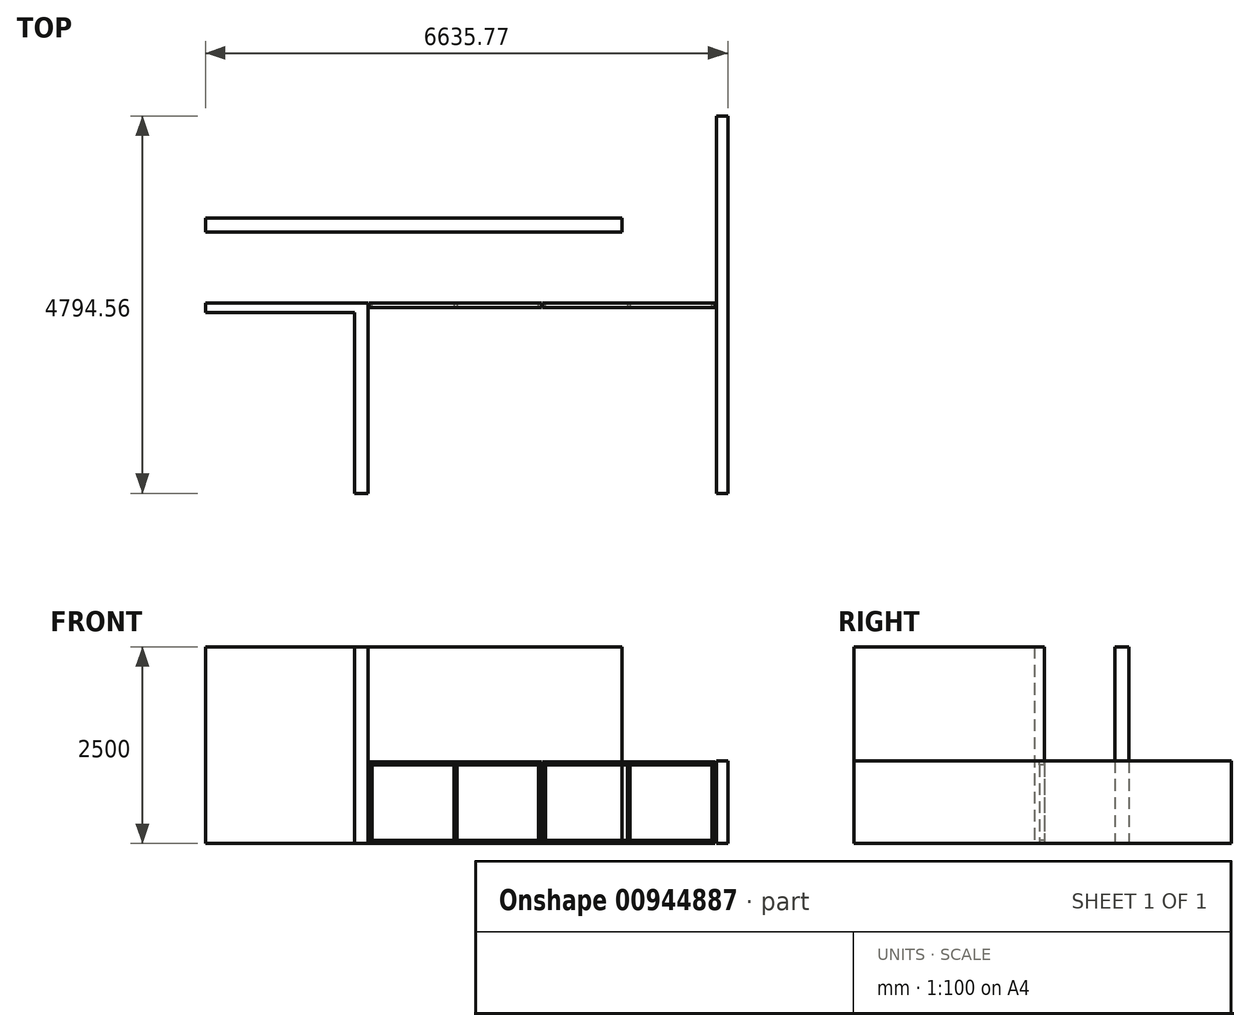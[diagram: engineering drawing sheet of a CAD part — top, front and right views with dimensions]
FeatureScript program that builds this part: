
annotation { "Feature Type Name" : "Feature", "Feature Type Description" : "" }
export const myFeature = defineFeature(function(context is Context, id is Id, definition is map)
    precondition{}
    {
        {
            var Q0;
            Q0=qCreatedBy(makeId("Top.planeOp"),FACE);
            var sketch = newSketch(context, id + "F0", { "sketchPlane" : qUnion([Q0])});
            skLineSegment(sketch, "E0.bottom", {"start": v(-2402.82, -1054.36) * mm, "end": v(-2228.62, -1054.36) * mm});
            skLineSegment(sketch, "E0.top", {"start": v(-2402.82, 1365.64) * mm, "end": v(-2228.62, 1365.64) * mm});
            skLineSegment(sketch, "E0.left", {"start": v(-2402.82, -1054.36) * mm, "end": v(-2402.82, 1365.64) * mm});
            skLineSegment(sketch, "E0.right", {"start": v(-2228.62, -1054.36) * mm, "end": v(-2228.62, 1365.64) * mm});
            skLineSegment(sketch, "E1.bottom", {"start": v(2338.5, -1054.36) * mm, "end": v(2191.38, -1054.36) * mm});
            skLineSegment(sketch, "E1.top", {"start": v(2338.5, 1365.64) * mm, "end": v(2191.38, 1365.64) * mm});
            skLineSegment(sketch, "E1.left", {"start": v(2338.5, -1054.36) * mm, "end": v(2338.5, 1365.64) * mm});
            skLineSegment(sketch, "E1.right", {"start": v(2191.38, -1054.36) * mm, "end": v(2191.38, 1365.64) * mm});
            skLineSegment(sketch, "E2.left", {"start": v(-2228.62, 1365.64) * mm, "end": v(-2228.62, 1323) * mm});
            skLineSegment(sketch, "E3.bottom", {"start": v(991.38, 2441.57) * mm, "end": v(-4297.27, 2441.57) * mm});
            skLineSegment(sketch, "E3.top", {"start": v(991.38, 2265.64) * mm, "end": v(-4297.27, 2265.64) * mm});
            skLineSegment(sketch, "E3.left", {"start": v(991.38, 2441.57) * mm, "end": v(991.38, 2265.64) * mm});
            skLineSegment(sketch, "E3.right", {"start": v(-4297.27, 2441.57) * mm, "end": v(-4297.27, 2265.64) * mm});
            skLineSegment(sketch, "E4.bottom", {"start": v(-2402.82, 1365.64) * mm, "end": v(-4297.27, 1365.64) * mm});
            skLineSegment(sketch, "E4.top", {"start": v(-2402.82, 1241.32) * mm, "end": v(-4297.27, 1241.32) * mm});
            skLineSegment(sketch, "E4.left", {"start": v(-2402.82, 1365.64) * mm, "end": v(-2402.82, 1241.32) * mm});
            skLineSegment(sketch, "E4.right", {"start": v(-4297.27, 1365.64) * mm, "end": v(-4297.27, 1241.32) * mm});
            skLineSegment(sketch, "E5.top", {"start": v(2338.5, 3740.2) * mm, "end": v(2191.38, 3740.2) * mm});
            skLineSegment(sketch, "E5.left", {"start": v(2338.5, 1365.64) * mm, "end": v(2338.5, 3740.2) * mm});
            skLineSegment(sketch, "E5.right", {"start": v(2191.38, 1365.64) * mm, "end": v(2191.38, 3740.2) * mm});
            skLineSegment(sketch, "E6.bottom", {"start": v(991.38, 2441.57) * mm, "end": v(764.32, 2441.57) * mm});
            skLineSegment(sketch, "E6.top", {"start": v(991.38, 3740.2) * mm, "end": v(764.32, 3740.2) * mm});
            skLineSegment(sketch, "E6.left", {"start": v(991.38, 2441.57) * mm, "end": v(991.38, 3740.2) * mm});
            skLineSegment(sketch, "E6.right", {"start": v(764.32, 2441.57) * mm, "end": v(764.32, 3740.2) * mm});
            skSolve(sketch);
        }
        {
            var Q0;
            Q0=makeQuery(id+"F0.imprint","IMPRINT",FACE,{"disambiguationData":[TD([[makeQuery(id+"F0.imprint","IMPRINT",EDGE,{"derivedFrom":sQuery(id+"F0.wireOp",EDGE,"E0.bottom")}),1.0]])]});
            var Q1;
            Q1=makeQuery(id+"F0.imprint","IMPRINT",FACE,{"disambiguationData":[TD([[makeQuery(id+"F0.imprint","IMPRINT",EDGE,{"derivedFrom":sQuery(id+"F0.wireOp",EDGE,"E3.bottom")}),1.0]])]});
            var Q2;
            Q2=makeQuery(id+"F0.imprint","IMPRINT",FACE,{"disambiguationData":[TD([[makeQuery(id+"F0.imprint","IMPRINT",EDGE,{"derivedFrom":sQuery(id+"F0.wireOp",EDGE,"E4.bottom")}),1.0]])]});
            var Q3;
            Q3=makeQuery(id+"F0.imprint","IMPRINT",FACE,{"disambiguationData":[TD([[makeQuery(id+"F0.imprint","IMPRINT",EDGE,{"derivedFrom":sQuery(id+"F0.wireOp",EDGE,"E6.bottom")}),-1.0]])]});
            extrude(context, id + "F1", {"entities" : qUnion([Q0, Q1, Q2, Q3]), "depth" : 2500 * mm, "offsetDistance" : 25 * mm});
        }
        {
            var Q0;
            Q0=makeQuery(id+"F0.imprint","IMPRINT",FACE,{"disambiguationData":[TD([[makeQuery(id+"F0.imprint","IMPRINT",EDGE,{"derivedFrom":sQuery(id+"F0.wireOp",EDGE,"E1.bottom")}),-1.0]])]});
            var Q1;
            Q1=makeQuery(id+"F0.imprint","IMPRINT",FACE,{"disambiguationData":[TD([[makeQuery(id+"F0.imprint","IMPRINT",EDGE,{"derivedFrom":sQuery(id+"F0.wireOp",EDGE,"E1.top")}),-1.0]])]});
            extrude(context, id + "F2", {"entities" : qUnion([Q0, Q1]), "depth" : 1050 * mm, "offsetDistance" : 25 * mm});
        }
        {
            var Q0;
            Q0=qCreatedBy(makeId("Top.planeOp"),FACE);
            var sketch = newSketch(context, id + "F3", { "sketchPlane" : qUnion([Q0])});
            skLineSegment(sketch, "E7.0", {"start": v(-2228.62, -1054.36) * mm, "end": v(-2228.62, -1054.36) * mm});
            skLineSegment(sketch, "E8.bottom", {"start": v(-2220.12, 1302.64) * mm, "end": v(-25.12, 1302.64) * mm});
            skLineSegment(sketch, "E8.top", {"start": v(-2220.12, 1365.64) * mm, "end": v(-25.12, 1365.64) * mm});
            skLineSegment(sketch, "E8.left", {"start": v(-2228.62, 1302.64) * mm, "end": v(-2228.62, 1365.64) * mm});
            skLineSegment(sketch, "E8.right", {"start": v(2177.38, 1302.64) * mm, "end": v(2177.38, 1365.64) * mm});
            skPoint(sketch, "E9", {"position": v(-25.12, 1365.64) * mm});
            skPoint(sketch, "E10", {"position": v(-17.62, 1365.64) * mm});
            skLineSegment(sketch, "E11", {"start": v(-17.62, 1365.64) * mm, "end": v(-17.62, 1302.64) * mm});
            skLineSegment(sketch, "E12", {"start": v(-25.12, 1365.64) * mm, "end": v(-25.12, 1302.64) * mm});
            skLineSegment(sketch, "E13.trimOffspring", {"start": v(-17.62, 1302.64) * mm, "end": v(2177.38, 1302.64) * mm});
            skLineSegment(sketch, "E14.trimOffspring", {"start": v(-17.62, 1365.64) * mm, "end": v(2177.38, 1365.64) * mm});
            skLineSegment(sketch, "E15", {"start": v(-2220.12, 1365.64) * mm, "end": v(-2220.12, 1302.64) * mm});
            skLineSegment(sketch, "E16", {"start": v(-17.62, 1365.64) * mm, "end": v(-25.12, 1365.64) * mm, "construction": true});
            skPoint(sketch, "E17", {"position": v(-21.37, 1365.64) * mm});
            skSolve(sketch);
        }
        {
            var Q0;
            Q0=makeQuery(id+"F3.imprint","IMPRINT",FACE,{"disambiguationData":[TD([[makeQuery(id+"F3.imprint","IMPRINT",EDGE,{"derivedFrom":sQuery(id+"F3.wireOp",EDGE,"E8.right")}),1.0]])]});
            extrude(context, id + "F4", {"entities" : qUnion([Q0]), "depth" : 38 * mm, "offsetDistance" : 25 * mm});
        }
        {
            var Q0;
            Q0=makeQuery(id+"F3.imprint","IMPRINT",FACE,{"disambiguationData":[TD([[makeQuery(id+"F3.imprint","IMPRINT",EDGE,{"derivedFrom":sQuery(id+"F3.wireOp",EDGE,"E8.bottom")}),1.0]])]});
            extrude(context, id + "F5", {"entities" : qUnion([Q0]), "depth" : 38 * mm, "offsetDistance" : 25 * mm});
        }
        {
            var Q0;
            Q0=makeQuery(id+"F4.opExtrude","CAP_FACE",FACE,{"disambiguationData":[OSD([sQuery(id+"F3.wireOp",EDGE,"E8.right"),sQuery(id+"F3.wireOp",EDGE,"E11"),sQuery(id+"F3.wireOp",EDGE,"E13.trimOffspring"),sQuery(id+"F3.wireOp",EDGE,"E14.trimOffspring")])],"isStart":false});
            var sketch = newSketch(context, id + "F6", { "sketchPlane" : qUnion([Q0])});
            skLineSegment(sketch, "E18.bottom", {"start": v(2177.38, 1302.64) * mm, "end": v(2139.38, 1302.64) * mm});
            skLineSegment(sketch, "E18.top", {"start": v(2177.38, 1365.64) * mm, "end": v(2139.38, 1365.64) * mm});
            skLineSegment(sketch, "E18.left", {"start": v(2177.38, 1302.64) * mm, "end": v(2177.38, 1365.64) * mm});
            skLineSegment(sketch, "E18.right", {"start": v(2139.38, 1302.64) * mm, "end": v(2139.38, 1365.64) * mm});
            skLineSegment(sketch, "E19.bottom", {"start": v(-17.62, 1302.64) * mm, "end": v(20.38, 1302.64) * mm});
            skLineSegment(sketch, "E19.top", {"start": v(-17.62, 1365.64) * mm, "end": v(20.38, 1365.64) * mm});
            skLineSegment(sketch, "E19.left", {"start": v(-17.62, 1302.64) * mm, "end": v(-17.62, 1365.64) * mm});
            skLineSegment(sketch, "E19.right", {"start": v(20.38, 1302.64) * mm, "end": v(20.38, 1365.64) * mm});
            skLineSegment(sketch, "E20.bottom", {"start": v(-25.12, 1302.64) * mm, "end": v(-63.12, 1302.64) * mm});
            skLineSegment(sketch, "E20.top", {"start": v(-25.12, 1365.64) * mm, "end": v(-63.12, 1365.64) * mm});
            skLineSegment(sketch, "E20.left", {"start": v(-25.12, 1302.64) * mm, "end": v(-25.12, 1365.64) * mm});
            skLineSegment(sketch, "E20.right", {"start": v(-63.12, 1302.64) * mm, "end": v(-63.12, 1365.64) * mm});
            skLineSegment(sketch, "E21.bottom", {"start": v(-2182.12, 1302.64) * mm, "end": v(-2220.12, 1302.64) * mm});
            skLineSegment(sketch, "E21.top", {"start": v(-2182.12, 1365.64) * mm, "end": v(-2220.12, 1365.64) * mm});
            skLineSegment(sketch, "E21.left", {"start": v(-2182.12, 1302.64) * mm, "end": v(-2182.12, 1365.64) * mm});
            skLineSegment(sketch, "E21.right", {"start": v(-2220.12, 1302.64) * mm, "end": v(-2220.12, 1365.64) * mm});
            skLineSegment(sketch, "E22.bottom", {"start": v(1098.88, 1365.64) * mm, "end": v(1060.88, 1365.64) * mm});
            skLineSegment(sketch, "E22.top", {"start": v(1098.88, 1302.64) * mm, "end": v(1060.88, 1302.64) * mm});
            skLineSegment(sketch, "E22.left", {"start": v(1060.88, 1365.64) * mm, "end": v(1060.88, 1302.64) * mm});
            skLineSegment(sketch, "E22.right", {"start": v(1098.88, 1365.64) * mm, "end": v(1098.88, 1302.64) * mm});
            skLineSegment(sketch, "E23.bottom", {"start": v(-1103.62, 1365.64) * mm, "end": v(-1141.62, 1365.64) * mm});
            skLineSegment(sketch, "E23.top", {"start": v(-1103.62, 1302.64) * mm, "end": v(-1141.62, 1302.64) * mm});
            skLineSegment(sketch, "E23.left", {"start": v(-1103.62, 1365.64) * mm, "end": v(-1103.62, 1302.64) * mm});
            skLineSegment(sketch, "E23.right", {"start": v(-1141.62, 1365.64) * mm, "end": v(-1141.62, 1302.64) * mm});
            skPoint(sketch, "E24", {"position": v(1079.88, 1302.64) * mm});
            skPoint(sketch, "E25", {"position": v(-1122.62, 1302.64) * mm});
            skSolve(sketch);
        }
        {
            var Q0;
            Q0 = qSketchRegion(id + "F6", true);
            extrude(context, id + "F7", {"entities" : qUnion([Q0]), "depth" : 960 * mm, "offsetDistance" : 25 * mm});
        }
        {
            var Q0;
            Q0=makeQuery(id+"F7.opExtrude","CAP_FACE",FACE,{"disambiguationData":[OSD([sQuery(id+"F6.wireOp",EDGE,"E18.bottom"),sQuery(id+"F6.wireOp",EDGE,"E18.top"),sQuery(id+"F6.wireOp",EDGE,"E18.left"),sQuery(id+"F6.wireOp",EDGE,"E18.right")])],"isStart":false});
            var Q1;
            Q1=makeQuery(id+"F7.opExtrude","CAP_FACE",FACE,{"disambiguationData":[OSD([sQuery(id+"F6.wireOp",EDGE,"E18.bottom"),sQuery(id+"F6.wireOp",EDGE,"E18.top"),sQuery(id+"F6.wireOp",EDGE,"E18.left"),sQuery(id+"F6.wireOp",EDGE,"E18.right")])],"isStart":true});
            cPlane(context, id + "F8", {"entities" : qUnion([Q0, Q1]), "cplaneType" : CPlaneType.MID_PLANE, "offset" : 25 * mm, "width" : 150 * mm, "height" : 150 * mm});
        }
        {
            var Q0;
            Q0=makeQuery(id+"F4.opExtrude","SWEPT_BODY",BODY,{"disambiguationData":[OSD([sQuery(id+"F3.wireOp",EDGE,"E8.right"),sQuery(id+"F3.wireOp",EDGE,"E11"),sQuery(id+"F3.wireOp",EDGE,"E13.trimOffspring"),sQuery(id+"F3.wireOp",EDGE,"E14.trimOffspring")])]});
            var Q1;
            Q1=makeQuery(id+"F5.opExtrude","SWEPT_BODY",BODY,{"disambiguationData":[OSD([sQuery(id+"F3.wireOp",EDGE,"E8.bottom"),sQuery(id+"F3.wireOp",EDGE,"E8.top"),sQuery(id+"F3.wireOp",EDGE,"E12"),sQuery(id+"F3.wireOp",EDGE,"E15")])]});
            var Q2;
            Q2=qCreatedBy(id+"F8.planeOp",FACE);
            mirror(context, id + "F9", {"entities" : qUnion([Q0, Q1]), "mirrorPlane" : qUnion([Q2])});
        }
    });
